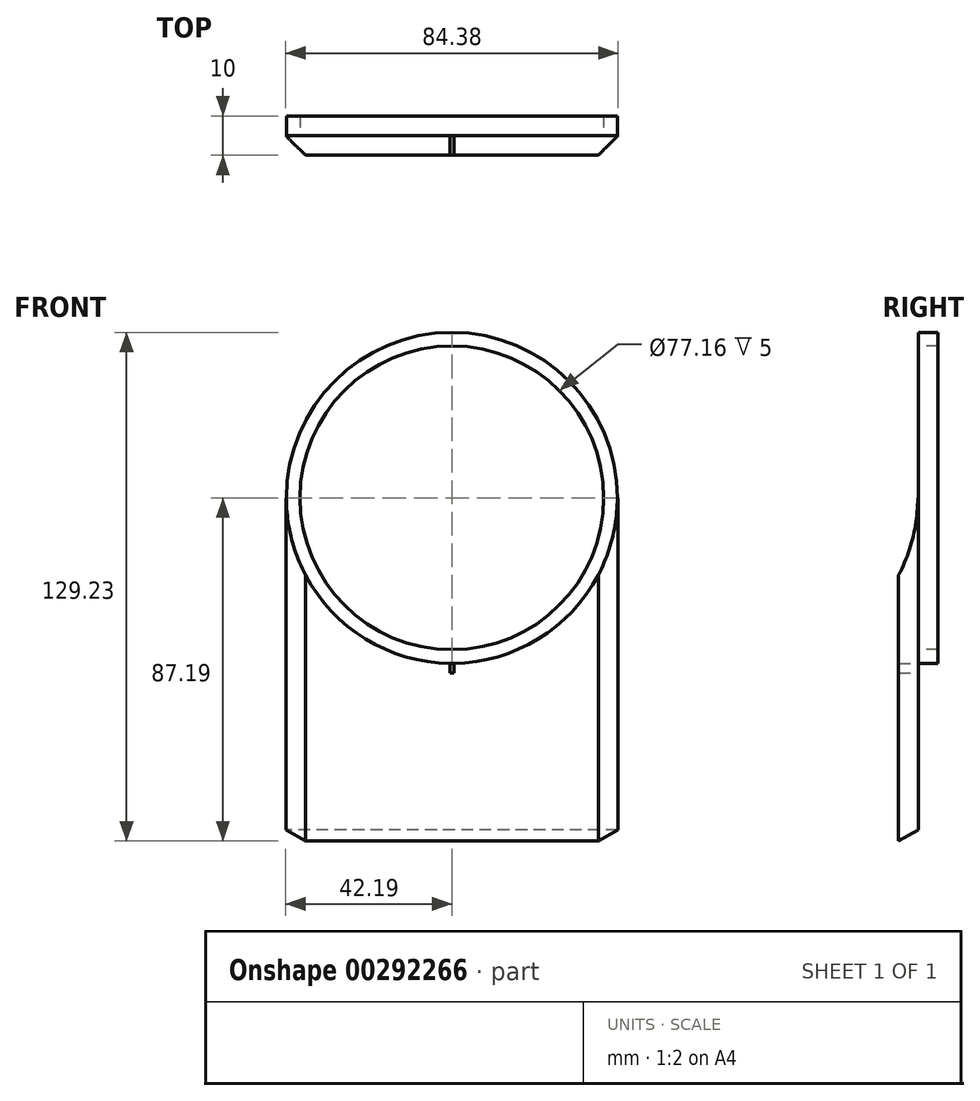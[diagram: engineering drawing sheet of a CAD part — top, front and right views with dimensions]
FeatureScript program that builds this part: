
annotation { "Feature Type Name" : "Feature", "Feature Type Description" : "" }
export const myFeature = defineFeature(function(context is Context, id is Id, definition is map)
    precondition{}
    {
        {
            var Q0;
            Q0=qCreatedBy(makeId("Front.planeOp"),FACE);
            var sketch = newSketch(context, id + "F0", { "sketchPlane" : qUnion([Q0])});
            skPoint(sketch, "E0.middle", {"position": v(0, 0) * mm});
            skLineSegment(sketch, "E1.bottom", {"start": v(-24, 24) * mm, "end": v(24, 24) * mm});
            skLineSegment(sketch, "E2.bottom", {"start": v(12.5, -24) * mm, "end": v(-12.5, -24) * mm});
            skLineSegment(sketch, "E2.top", {"start": v(12.5, -28) * mm, "end": v(-12.5, -28) * mm});
            skLineSegment(sketch, "E2.left", {"start": v(12.5, -24) * mm, "end": v(12.5, -28) * mm});
            skLineSegment(sketch, "E2.right", {"start": v(-12.5, -24) * mm, "end": v(-12.5, -28) * mm});
            skCircle(sketch, "E3", {"center": v(-24, 24) * mm, "radius": 2 * mm});
            skCircle(sketch, "E4", {"center": v(24, 24) * mm, "radius": 2 * mm});
            skCircle(sketch, "E5", {"center": v(24, -24) * mm, "radius": 2 * mm});
            skCircle(sketch, "E6", {"center": v(-24, -24) * mm, "radius": 2 * mm});
            skCircle(sketch, "E7", {"center": v(0, 0) * mm, "radius": 27.06 * mm});
            skSolve(sketch);
        }
        {
            var Q0;
            Q0=qCreatedBy(makeId("Front.planeOp"),FACE);
            var sketch = newSketch(context, id + "F1", { "sketchPlane" : qUnion([Q0])});
            skCircle(sketch, "E8", {"center": v(0, 0) * mm, "radius": 42.04 * mm});
            skCircle(sketch, "E9", {"center": v(0, 0) * mm, "radius": 42.19 * mm});
            skSolve(sketch);
        }
        {
            var Q0;
            Q0=qCreatedBy(makeId("Front.planeOp"),FACE);
            var sketch = newSketch(context, id + "F2", { "sketchPlane" : qUnion([Q0])});
            skCircle(sketch, "E10", {"center": v(0, 0) * mm, "radius": 38.58 * mm});
            skSolve(sketch);
        }
        {
            var Q0;
            Q0=makeQuery(id+"F1.imprint","IMPRINT",FACE,{"disambiguationData":[TD([[makeQuery(id+"F1.imprint","IMPRINT",EDGE,{"derivedFrom":sQuery(id+"F1.wireOp",EDGE,"E8")}),1.0]])]});
            extrude(context, id + "F3", {"entities" : qUnion([Q0]), "endBound" : BoundingType.SYMMETRIC, "depth" : 10 * mm});
        }
        {
            var Q0;
            Q0 = qSketchRegion(id + "F2", true);
            extrude(context, id + "F4", {"entities" : qUnion([Q0]), "operationType" : NewBodyOperationType.REMOVE, "oppositeDirection" : true, "depth" : 5 * mm});
        }
        {
            var Q0;
            Q0 = qSketchRegion(id + "F0", true);
            extrude(context, id + "F5", {"entities" : qUnion([Q0]), "operationType" : NewBodyOperationType.REMOVE, "depth" : 25 * mm});
        }
        {
            var Q0;
            Q0=qCreatedBy(makeId("Front.planeOp"),FACE);
            var sketch = newSketch(context, id + "F6", { "sketchPlane" : qUnion([Q0])});
            skLineSegment(sketch, "E11.bottom", {"start": v(-42.19, 0) * mm, "end": v(42.19, 0) * mm});
            skLineSegment(sketch, "E11.top", {"start": v(-42.19, -87.19) * mm, "end": v(42.19, -87.19) * mm});
            skLineSegment(sketch, "E11.left", {"start": v(-42.19, 0) * mm, "end": v(-42.19, -87.19) * mm});
            skLineSegment(sketch, "E11.right", {"start": v(42.19, 0) * mm, "end": v(42.19, -87.19) * mm});
            skPoint(sketch, "E12.centerSnap0", {"position": v(0, -87.19) * mm});
            skLineSegment(sketch, "E13.bottom", {"start": v(-0.5, -39.5) * mm, "end": v(0.5, -39.5) * mm});
            skLineSegment(sketch, "E13.top", {"start": v(-0.5, -44.5) * mm, "end": v(0.5, -44.5) * mm});
            skLineSegment(sketch, "E13.left", {"start": v(-0.5, -39.5) * mm, "end": v(-0.5, -44.5) * mm});
            skLineSegment(sketch, "E13.right", {"start": v(0.5, -39.5) * mm, "end": v(0.5, -44.5) * mm});
            skPoint(sketch, "E13.middle", {"position": v(0, -42) * mm});
            skSolve(sketch);
        }
        {
            var Q0;
            Q0 = qSketchRegion(id + "F6", true);
            extrude(context, id + "F7", {"entities" : qUnion([Q0]), "depth" : 5 * mm});
        }
        {
            var Q0;
            Q0=makeQuery(id+"F1.imprint","IMPRINT",FACE,{"disambiguationData":[TD([[makeQuery(id+"F1.imprint","IMPRINT",EDGE,{"derivedFrom":sQuery(id+"F1.wireOp",EDGE,"E8")}),1.0]])]});
            var Q1;
            Q1=sQuery(id+"F1.wireOp",EDGE,"E9");
            extrude(context, id + "F8", {"entities" : qUnion([Q0]), "operationType" : NewBodyOperationType.REMOVE, "surfaceEntities" : qUnion([Q1]), "depth" : 5 * mm});
        }
        {
            var Q0;
            Q0=makeQuery(id+"F7.opExtrude","CAP_EDGE",EDGE,{"disambiguationData":[OSD([sQuery(id+"F6.wireOp",EDGE,"E11.top")])],"isStart":true});
            chamfer(context, id + "F9", {"entities" : qUnion([Q0]), "chamferType" : ChamferType.OFFSET_ANGLE, "width" : 5 * mm, "oppositeDirection" : false, "angle" : 30 * degree, "tangentPropagation" : true});
        }
        {
            var Q0;
            Q0=makeQuery(id+"F7.opExtrude","CAP_EDGE",EDGE,{"disambiguationData":[OSD([sQuery(id+"F6.wireOp",EDGE,"E11.left")])],"isStart":false});
            var Q1;
            Q1=makeQuery(id+"F7.opExtrude","CAP_EDGE",EDGE,{"disambiguationData":[OSD([sQuery(id+"F6.wireOp",EDGE,"E11.right")])],"isStart":false});
            chamfer(context, id + "F10", {"entities" : qUnion([Q0, Q1]), "width" : 5 * mm, "tangentPropagation" : true});
        }
    });
